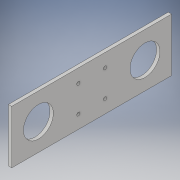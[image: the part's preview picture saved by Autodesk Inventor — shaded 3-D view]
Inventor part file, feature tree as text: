
AUTODESK INVENTOR PART (.ipt)
format: ipt  version: 2017 (Build 210142000, 142)  size: 109,056 bytes
history: native  units: in
note: dims shown in document units (in); Inventor stores cm internally (conversion verified against a paired STEP export)
features: extrude x1, sketch x1
ambient origin geometry x8: Origin, YZ Plane, XZ Plane, XY Plane, X Axis, Y Axis, Z Axis, Center Point
bodies: Body1 (feature_tree)
feature tree (2):
  extrude  "Extrusion2"  Depth=6.0in
  sketch  "Sketch1"  dims[d11=2.0in d12=6.0in d13=1.0in d14=1.125in d22=0.5in d23=0.5in d24=0.125in d25=0.125in d26=0.0in]
